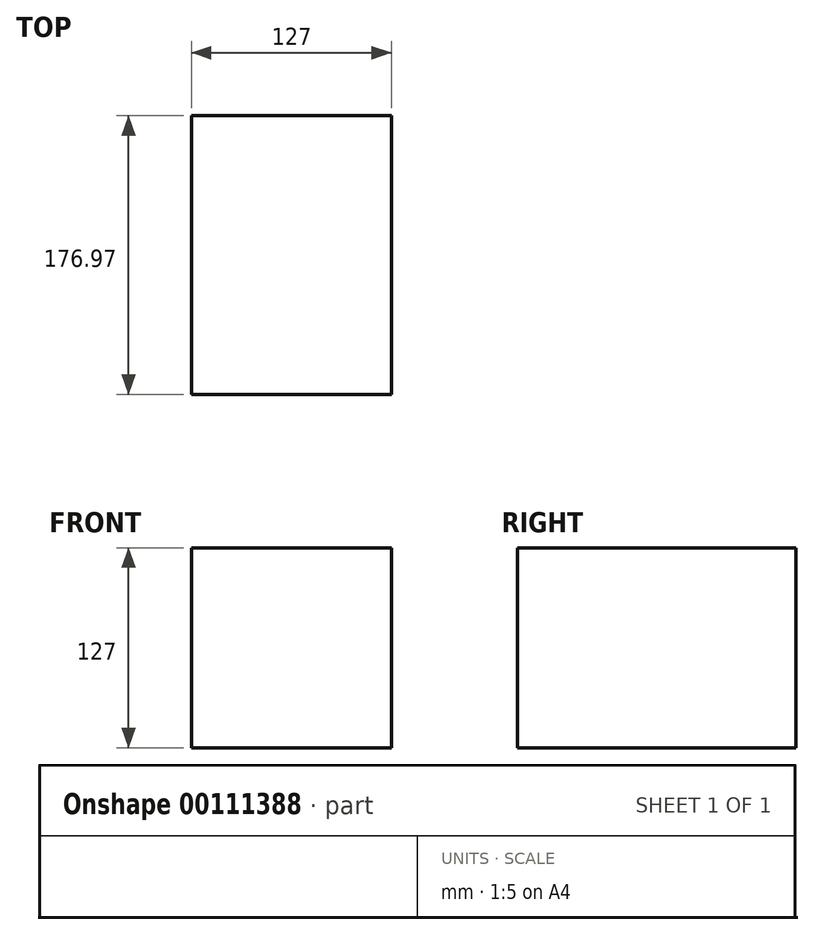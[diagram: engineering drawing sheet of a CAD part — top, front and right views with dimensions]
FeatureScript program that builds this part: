
annotation { "Feature Type Name" : "Feature", "Feature Type Description" : "" }
export const myFeature = defineFeature(function(context is Context, id is Id, definition is map)
    precondition{}
    {
        {
            var Q0;
            Q0=qCreatedBy(makeId("Front.planeOp"),FACE);
            var sketch = newSketch(context, id + "F0", { "sketchPlane" : qUnion([Q0])});
            skLineSegment(sketch, "E0.bottom", {"start": v(-68.86, 76) * mm, "end": v(58.14, 76) * mm});
            skLineSegment(sketch, "E0.top", {"start": v(-68.86, -51) * mm, "end": v(58.14, -51) * mm});
            skLineSegment(sketch, "E0.left", {"start": v(-68.86, 76) * mm, "end": v(-68.86, -51) * mm});
            skLineSegment(sketch, "E0.right", {"start": v(58.14, 76) * mm, "end": v(58.14, -51) * mm});
            skSolve(sketch);
        }
        {
            var Q0;
            Q0=makeQuery(id+"F0.imprint","IMPRINT",FACE,{"disambiguationData":[TD([[makeQuery(id+"F0.imprint","IMPRINT",EDGE,{"derivedFrom":sQuery(id+"F0.wireOp",EDGE,"E0.bottom")}),-1.0]])]});
            extrude(context, id + "F1", {"entities" : qUnion([Q0]), "depth" : 176.97 * mm});
        }
    });
